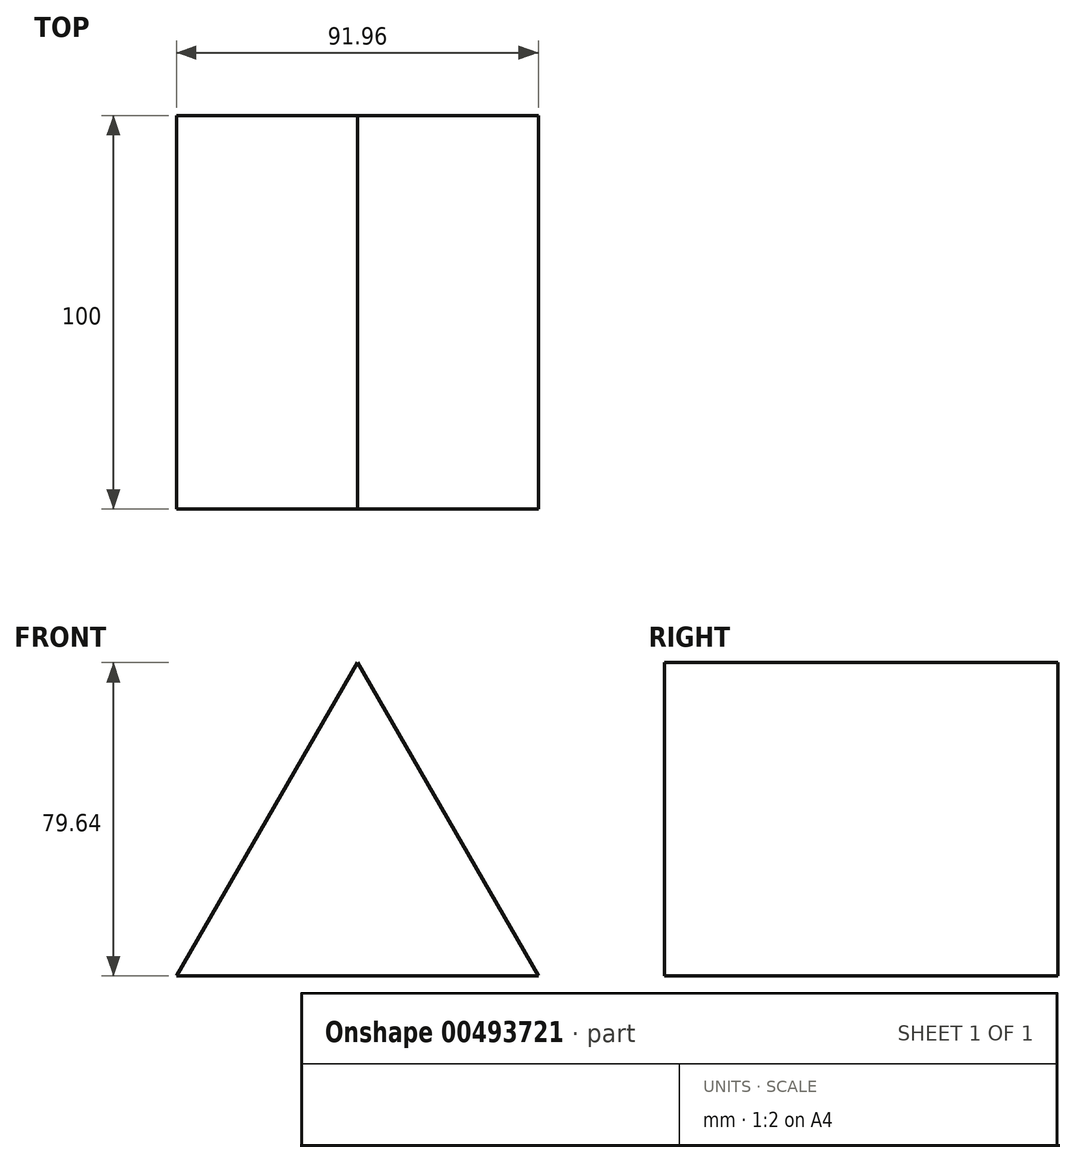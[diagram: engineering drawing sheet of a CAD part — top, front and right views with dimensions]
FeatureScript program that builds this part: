
annotation { "Feature Type Name" : "Feature", "Feature Type Description" : "" }
export const myFeature = defineFeature(function(context is Context, id is Id, definition is map)
    precondition{}
    {
        {
            var Q0;
            Q0=qCreatedBy(makeId("Front.planeOp"),FACE);
            var sketch = newSketch(context, id + "F0", { "sketchPlane" : qUnion([Q0])});
            skCircle(sketch, "E0.cCircle", {"center": v(0, 0) * mm, "radius": 53.1 * mm, "construction": true});
            skLineSegment(sketch, "E0.0", {"start": v(0, 53.1) * mm, "end": v(45.98, -26.55) * mm});
            skLineSegment(sketch, "E0.1", {"start": v(45.98, -26.55) * mm, "end": v(-45.98, -26.55) * mm});
            skLineSegment(sketch, "E0.2", {"start": v(-45.98, -26.55) * mm, "end": v(0, 53.1) * mm});
            skSolve(sketch);
        }
        {
            var Q0;
            Q0=makeQuery(id+"F0.imprint","IMPRINT",FACE,{"disambiguationData":[TD([[makeQuery(id+"F0.imprint","IMPRINT",EDGE,{"derivedFrom":sQuery(id+"F0.wireOp",EDGE,"E0.0")}),-1.0]])]});
            extrude(context, id + "F1", {"entities" : qUnion([Q0]), "endBound" : BoundingType.SYMMETRIC, "depth" : 100 * mm});
        }
    });
